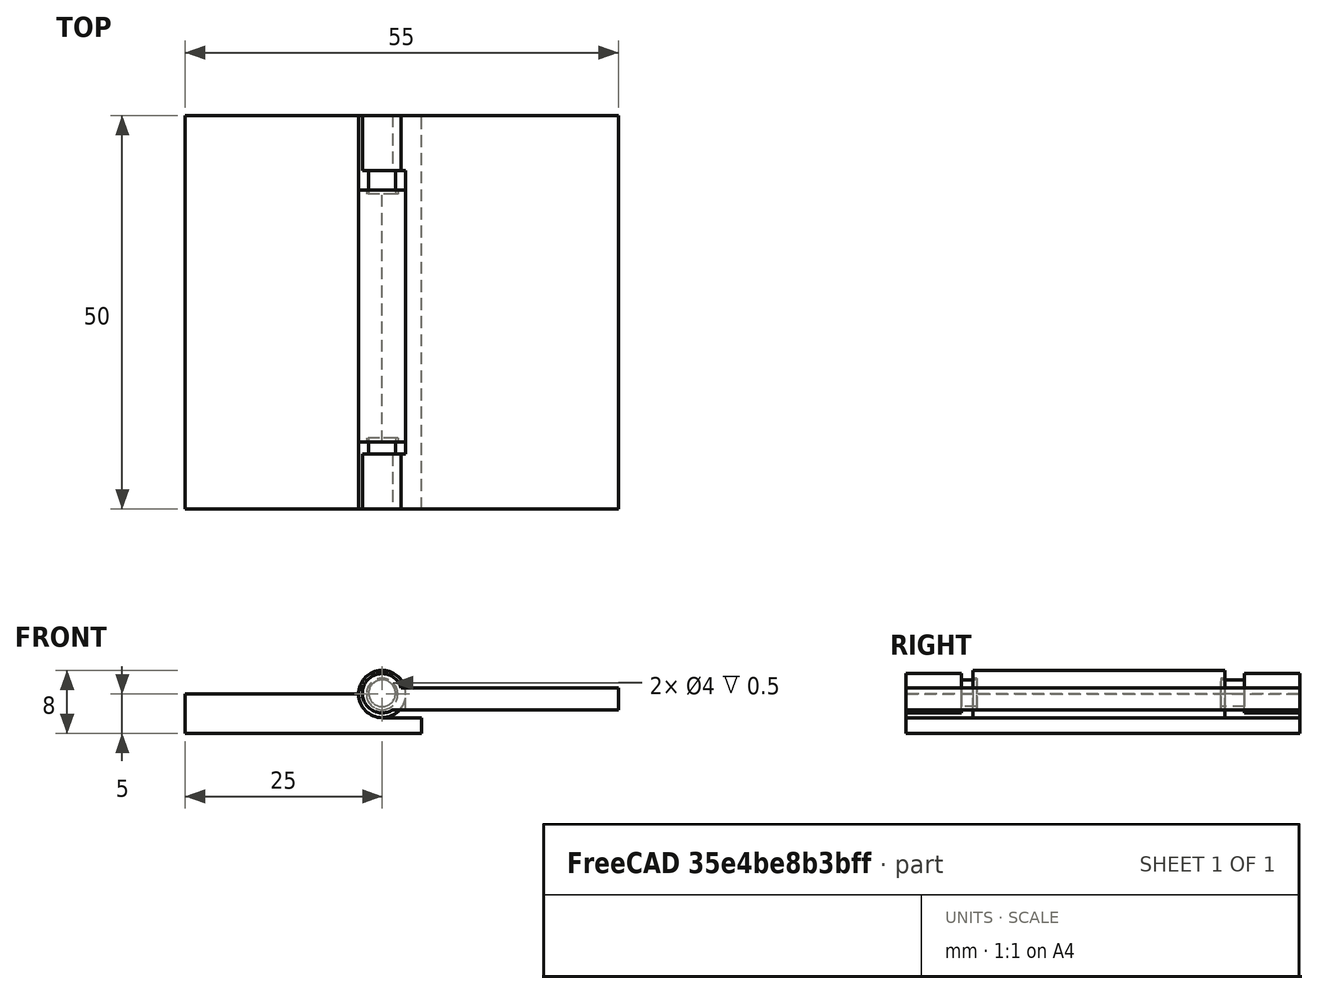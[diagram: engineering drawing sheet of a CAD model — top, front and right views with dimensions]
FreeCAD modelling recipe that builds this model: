
FCSTD DOCUMENT  (FreeCAD 0.16R6712 (Git))
Label: Hinge03
License: All rights reserved
LicenseURL: http://en.wikipedia.org/wiki/All_rights_reserved
objects: Part::Cylinder×9, Part::Cut×6, Part::MultiFuse×5, Part::Box×4
note: 24 computed .brp shape members not serialized (recipe doc carries the construction recipe); baked Part::Feature solids carry a one-line shape summary decoded from their .brp

FEATURE [Part::Box] Box  label="Cube"
  Height = 5
  Length = 30
  Width = 50
FEATURE [Part::Cylinder] Cylinder
  Angle = 360
  Height = 33
  Placement = pos=(25,41.5,5) rot=(1,0,0;1.5708rad)
  Radius = 3
FEATURE [Part::Box] Box001  label="Cube001"
  Height = 3
  Length = 5
  Placement = pos=(25,0,2) rot=(0,0,1;0rad)
  Width = 50
FEATURE [Part::Cut] Cut
  Base = -> Box
  Tool = -> Box001
FEATURE [Part::MultiFuse] Fusion
  Shapes = -> [Cylinder,Cut]
FEATURE [Part::Cylinder] Cylinder001
  Angle = 360
  Height = 8.5
  Placement = pos=(25,8.5,5) rot=(1,0,0;1.5708rad)
  Radius = 3
FEATURE [Part::Cylinder] Cylinder002
  Angle = 360
  Height = 9.5
  Placement = pos=(25,50,5) rot=(1,0,0;1.5708rad)
  Radius = 3
FEATURE [Part::Cut] Cut001
  Base = -> Fusion
  Tool = -> Cylinder001
FEATURE [Part::Cut] Cut002
  Base = -> Cut001
  Tool = -> Cylinder002
FEATURE [Part::Box] Box002  label="Cube002"
  Height = 2.8
  Length = 30
  Placement = pos=(25,0,3) rot=(0,0,1;0rad)
  Width = 50
FEATURE [Part::Cylinder] Cylinder003
  Angle = 360
  Height = 7
  Placement = pos=(25,7,5.1) rot=(1,0,0;1.5708rad)
  Radius = 2.5
FEATURE [Part::Cylinder] Cylinder004
  Angle = 360
  Height = 7
  Placement = pos=(25,50,5.1) rot=(1,0,0;1.5708rad)
  Radius = 2.5
FEATURE [Part::Box] Box003  label="Cube003"
  Height = 3
  Length = 3
  Placement = pos=(25,7,3) rot=(0,0,1;0rad)
  Width = 36
FEATURE [Part::Cut] Cut003
  Base = -> Box002
  Tool = -> Box003
FEATURE [Part::MultiFuse] Fusion001
  Shapes = -> [Cut003,Cylinder003]
FEATURE [Part::MultiFuse] Fusion002
  Shapes = -> [Fusion001,Cylinder004]
FEATURE [Part::Cylinder] Cylinder005
  Angle = 360
  Height = 2
  Placement = pos=(25,9,5) rot=(1,0,0;1.5708rad)
  Radius = 2
FEATURE [Part::Cylinder] Cylinder006
  Angle = 360
  Height = 2
  Placement = pos=(25,42,5) rot=(1,0,0;1.5708rad)
  Radius = 2
FEATURE [Part::Cylinder] Cylinder007
  Angle = 360
  Height = 3
  Placement = pos=(25,9,5.1) rot=(1,0,0;1.5708rad)
  Radius = 1.7
FEATURE [Part::Cylinder] Cylinder008
  Angle = 360
  Height = 3
  Placement = pos=(25,43,5.1) rot=(1,0,0;1.5708rad)
  Radius = 1.7
FEATURE [Part::Cut] Cut004
  Base = -> Cut002
  Tool = -> Cylinder005
FEATURE [Part::Cut] Cut005
  Base = -> Cut004
  Tool = -> Cylinder006
FEATURE [Part::MultiFuse] Fusion003
  Shapes = -> [Fusion002,Cylinder007]
FEATURE [Part::MultiFuse] Fusion004
  Shapes = -> [Fusion003,Cylinder008]
